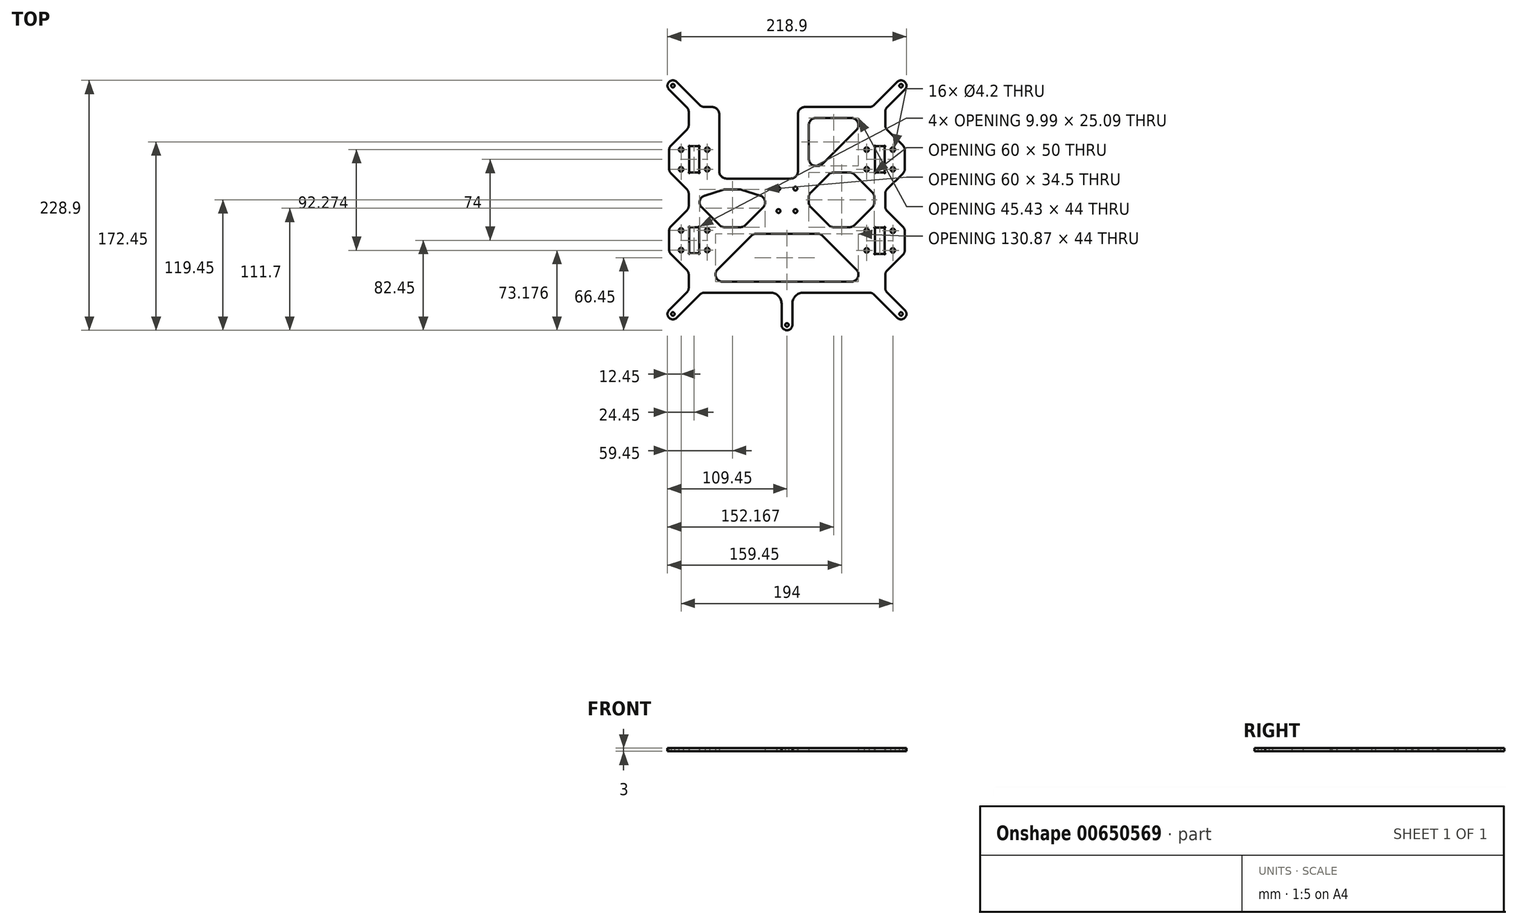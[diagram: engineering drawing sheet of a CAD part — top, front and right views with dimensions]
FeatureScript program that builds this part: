
annotation { "Feature Type Name" : "Feature", "Feature Type Description" : "" }
export const myFeature = defineFeature(function(context is Context, id is Id, definition is map)
    precondition{}
    {
        {
            var Q0;
            Q0=qCreatedBy(makeId("Top.planeOp"),FACE);
            var sketch = newSketch(context, id + "F0", { "sketchPlane" : qUnion([Q0])});
            skLineSegment(sketch, "E0", {"start": v(-106.24, 49.76) * mm, "end": v(-91.76, 64.24) * mm});
            skArc(sketch, "E1", {"start": v(-91.76, 64.24) * mm, "mid": v(-90.46, 66.19) * mm, "end": v(-90, 68.49) * mm});
            skLineSegment(sketch, "E2", {"start": v(-90, 68.49) * mm, "end": v(-90, 80.51) * mm});
            skArc(sketch, "E3", {"start": v(-90, 80.51) * mm, "mid": v(-90.46, 82.81) * mm, "end": v(-91.76, 84.76) * mm});
            skLineSegment(sketch, "E4", {"start": v(-91.76, 84.76) * mm, "end": v(-108, 101) * mm});
            skArc(sketch, "E5", {"start": v(-101, 108) * mm, "mid": v(-108, 108) * mm, "end": v(-108, 101) * mm});
            skLineSegment(sketch, "E6", {"start": v(-101, 108) * mm, "end": v(-79.76, 86.76) * mm});
            skArc(sketch, "E7", {"start": v(-79.76, 86.76) * mm, "mid": v(-77.81, 85.46) * mm, "end": v(-75.51, 85) * mm});
            skLineSegment(sketch, "E8", {"start": v(16.6, 85) * mm, "end": v(75.51, 85) * mm});
            skArc(sketch, "E9", {"start": v(75.51, 85) * mm, "mid": v(77.81, 85.46) * mm, "end": v(79.76, 86.76) * mm});
            skLineSegment(sketch, "E10", {"start": v(79.76, 86.76) * mm, "end": v(101, 108) * mm});
            skArc(sketch, "E11", {"start": v(108, 101) * mm, "mid": v(108, 108) * mm, "end": v(101, 108) * mm});
            skLineSegment(sketch, "E12", {"start": v(108, 101) * mm, "end": v(91.76, 84.76) * mm});
            skLineSegment(sketch, "E13", {"start": v(91.76, -84.76) * mm, "end": v(108, -101) * mm});
            skArc(sketch, "E14", {"start": v(101, -108) * mm, "mid": v(108, -108) * mm, "end": v(108, -101) * mm});
            skLineSegment(sketch, "E15", {"start": v(101, -108) * mm, "end": v(79.76, -86.76) * mm});
            skArc(sketch, "E16", {"start": v(79.76, -86.76) * mm, "mid": v(77.81, -85.46) * mm, "end": v(75.51, -85) * mm});
            skLineSegment(sketch, "E17", {"start": v(75.51, -85) * mm, "end": v(14.95, -85) * mm});
            skArc(sketch, "E18", {"start": v(-75.51, -85) * mm, "mid": v(-77.81, -85.46) * mm, "end": v(-79.76, -86.76) * mm});
            skLineSegment(sketch, "E19", {"start": v(-79.76, -86.76) * mm, "end": v(-101, -108) * mm});
            skArc(sketch, "E20", {"start": v(-108, -101) * mm, "mid": v(-108, -108) * mm, "end": v(-101, -108) * mm});
            skLineSegment(sketch, "E21", {"start": v(-108, -101) * mm, "end": v(-91.76, -84.76) * mm});
            skArc(sketch, "E22", {"start": v(-91.76, -84.76) * mm, "mid": v(-90.46, -82.81) * mm, "end": v(-90, -80.51) * mm});
            skLineSegment(sketch, "E23", {"start": v(-90, -80.51) * mm, "end": v(-90, -68.49) * mm});
            skArc(sketch, "E24", {"start": v(-90, -68.49) * mm, "mid": v(-90.46, -66.19) * mm, "end": v(-91.76, -64.24) * mm});
            skLineSegment(sketch, "E25", {"start": v(-91.76, -64.24) * mm, "end": v(-106.24, -49.76) * mm});
            skArc(sketch, "E26", {"start": v(-108, -45.51) * mm, "mid": v(-107.54, -47.81) * mm, "end": v(-106.24, -49.76) * mm});
            skLineSegment(sketch, "E27", {"start": v(-108, -45.51) * mm, "end": v(-108, -28.49) * mm});
            skArc(sketch, "E28", {"start": v(-106.24, -24.24) * mm, "mid": v(-107.54, -26.19) * mm, "end": v(-108, -28.49) * mm});
            skLineSegment(sketch, "E29", {"start": v(-106.24, -24.24) * mm, "end": v(-91.76, -9.76) * mm});
            skArc(sketch, "E30", {"start": v(-91.76, -9.76) * mm, "mid": v(-90.46, -7.81) * mm, "end": v(-90, -5.51) * mm});
            skLineSegment(sketch, "E31", {"start": v(-90, -5.51) * mm, "end": v(-90, 5.51) * mm});
            skArc(sketch, "E32", {"start": v(-90, 5.51) * mm, "mid": v(-90.46, 7.81) * mm, "end": v(-91.76, 9.76) * mm});
            skLineSegment(sketch, "E33", {"start": v(-91.76, 9.76) * mm, "end": v(-106.24, 24.24) * mm});
            skArc(sketch, "E34", {"start": v(-108, 28.49) * mm, "mid": v(-107.54, 26.19) * mm, "end": v(-106.24, 24.24) * mm});
            skLineSegment(sketch, "E35", {"start": v(-108, 28.49) * mm, "end": v(-108, 45.51) * mm});
            skArc(sketch, "E36", {"start": v(-106.24, 49.76) * mm, "mid": v(-107.54, 47.81) * mm, "end": v(-108, 45.51) * mm});
            skLineSegment(sketch, "E37", {"start": v(32.73, -32.93) * mm, "end": v(63.53, -63.73) * mm});
            skArc(sketch, "E38", {"start": v(58.87, -75) * mm, "mid": v(64.96, -70.93) * mm, "end": v(63.53, -63.73) * mm});
            skLineSegment(sketch, "E39", {"start": v(58.87, -75) * mm, "end": v(-58.87, -75) * mm});
            skArc(sketch, "E40", {"start": v(-63.53, -63.73) * mm, "mid": v(-64.96, -70.93) * mm, "end": v(-58.87, -75) * mm});
            skLineSegment(sketch, "E41", {"start": v(-63.53, -63.73) * mm, "end": v(-32.73, -32.93) * mm});
            skArc(sketch, "E42", {"start": v(-28.07, -31) * mm, "mid": v(-30.6, -31.5) * mm, "end": v(-32.73, -32.93) * mm});
            skLineSegment(sketch, "E43", {"start": v(-28.07, -31) * mm, "end": v(28.07, -31) * mm});
            skArc(sketch, "E44", {"start": v(32.73, -32.93) * mm, "mid": v(30.6, -31.5) * mm, "end": v(28.07, -31) * mm});
            skLineSegment(sketch, "E45", {"start": v(-55.4, 19.5) * mm, "end": v(3.4, 19.5) * mm});
            skLineSegment(sketch, "E46", {"start": v(-20, -2.35) * mm, "end": v(-20, -2.51) * mm});
            skArc(sketch, "E47", {"start": v(-21.76, -6.76) * mm, "mid": v(-20.46, -4.81) * mm, "end": v(-20, -2.51) * mm});
            skLineSegment(sketch, "E48", {"start": v(-21.76, -6.76) * mm, "end": v(-38.24, -23.24) * mm});
            skArc(sketch, "E49", {"start": v(-42.49, -25) * mm, "mid": v(-40.19, -24.54) * mm, "end": v(-38.24, -23.24) * mm});
            skLineSegment(sketch, "E50", {"start": v(-42.49, -25) * mm, "end": v(-57.51, -25) * mm});
            skArc(sketch, "E51", {"start": v(-61.76, -23.24) * mm, "mid": v(-59.81, -24.54) * mm, "end": v(-57.51, -25) * mm});
            skLineSegment(sketch, "E52", {"start": v(-61.76, -23.24) * mm, "end": v(-78.24, -6.76) * mm});
            skArc(sketch, "E53", {"start": v(-80, -2.51) * mm, "mid": v(-79.54, -4.81) * mm, "end": v(-78.24, -6.76) * mm});
            skLineSegment(sketch, "E54", {"start": v(-80, -2.51) * mm, "end": v(-80, -2.35) * mm});
            skLineSegment(sketch, "E55", {"start": v(38.24, -23.24) * mm, "end": v(21.76, -6.76) * mm});
            skArc(sketch, "E56", {"start": v(20, -2.51) * mm, "mid": v(20.46, -4.81) * mm, "end": v(21.76, -6.76) * mm});
            skLineSegment(sketch, "E57", {"start": v(20, -2.51) * mm, "end": v(20, 2.51) * mm});
            skArc(sketch, "E58", {"start": v(21.76, 6.76) * mm, "mid": v(20.46, 4.81) * mm, "end": v(20, 2.51) * mm});
            skLineSegment(sketch, "E59", {"start": v(21.76, 6.76) * mm, "end": v(38.24, 23.24) * mm});
            skArc(sketch, "E60", {"start": v(42.49, 25) * mm, "mid": v(40.19, 24.54) * mm, "end": v(38.24, 23.24) * mm});
            skArc(sketch, "E61", {"start": v(38.24, -23.24) * mm, "mid": v(40.19, -24.54) * mm, "end": v(42.49, -25) * mm});
            skLineSegment(sketch, "E62", {"start": v(-88.63, -49.05) * mm, "end": v(-81.37, -49.05) * mm});
            skLineSegment(sketch, "E63", {"start": v(-89.5, 48.18) * mm, "end": v(-89.5, 25.82) * mm});
            skArc(sketch, "E64", {"start": v(-89.75, 25.38) * mm, "mid": v(-89.57, 25.57) * mm, "end": v(-89.5, 25.82) * mm});
            skArc(sketch, "E65", {"start": v(-89.75, 25.38) * mm, "mid": v(-89.85, 24.6) * mm, "end": v(-89.07, 24.7) * mm});
            skArc(sketch, "E66", {"start": v(-88.63, 24.95) * mm, "mid": v(-88.88, 24.88) * mm, "end": v(-89.07, 24.7) * mm});
            skLineSegment(sketch, "E67", {"start": v(-88.63, 24.95) * mm, "end": v(-81.37, 24.95) * mm});
            skArc(sketch, "E68", {"start": v(-80.93, 24.7) * mm, "mid": v(-81.12, 24.88) * mm, "end": v(-81.37, 24.95) * mm});
            skArc(sketch, "E69", {"start": v(-80.93, 24.7) * mm, "mid": v(-80.15, 24.6) * mm, "end": v(-80.25, 25.38) * mm});
            skArc(sketch, "E70", {"start": v(-80.5, 25.82) * mm, "mid": v(-80.43, 25.57) * mm, "end": v(-80.25, 25.38) * mm});
            skLineSegment(sketch, "E71", {"start": v(-80.5, 25.82) * mm, "end": v(-80.5, 48.18) * mm});
            skArc(sketch, "E72", {"start": v(-80.25, 48.62) * mm, "mid": v(-80.43, 48.43) * mm, "end": v(-80.5, 48.18) * mm});
            skArc(sketch, "E73", {"start": v(-80.25, 48.62) * mm, "mid": v(-80.15, 49.4) * mm, "end": v(-80.93, 49.3) * mm});
            skArc(sketch, "E74", {"start": v(-81.37, 49.05) * mm, "mid": v(-81.12, 49.12) * mm, "end": v(-80.93, 49.3) * mm});
            skLineSegment(sketch, "E75", {"start": v(-81.37, 49.05) * mm, "end": v(-88.63, 49.05) * mm});
            skArc(sketch, "E76", {"start": v(-89.07, 49.3) * mm, "mid": v(-88.88, 49.12) * mm, "end": v(-88.63, 49.05) * mm});
            skArc(sketch, "E77", {"start": v(-89.07, 49.3) * mm, "mid": v(-89.85, 49.4) * mm, "end": v(-89.75, 48.62) * mm});
            skArc(sketch, "E78", {"start": v(-89.5, 48.18) * mm, "mid": v(-89.57, 48.43) * mm, "end": v(-89.75, 48.62) * mm});
            skCircle(sketch, "E79", {"center": v(-104.5, -104.5) * mm, "radius": 1.6 * mm});
            skCircle(sketch, "E80", {"center": v(-104.5, 104.5) * mm, "radius": 1.6 * mm});
            skCircle(sketch, "E81", {"center": v(-97, -28) * mm, "radius": 2.1 * mm});
            skCircle(sketch, "E82", {"center": v(-97, 28) * mm, "radius": 2.1 * mm});
            skCircle(sketch, "E83", {"center": v(-73, -28) * mm, "radius": 2.1 * mm});
            skCircle(sketch, "E84", {"center": v(-7.75, -10.25) * mm, "radius": 1.75 * mm});
            skCircle(sketch, "E85", {"center": v(7.75, -10.25) * mm, "radius": 1.75 * mm});
            skCircle(sketch, "E86", {"center": v(104.5, -104.5) * mm, "radius": 1.6 * mm});
            skCircle(sketch, "E87", {"center": v(104.5, 104.5) * mm, "radius": 1.6 * mm});
            skLineSegment(sketch, "E88", {"start": v(-89.5, -25.82) * mm, "end": v(-89.5, -48.18) * mm});
            skArc(sketch, "E89", {"start": v(-89.75, -48.62) * mm, "mid": v(-89.57, -48.43) * mm, "end": v(-89.5, -48.18) * mm});
            skArc(sketch, "E90", {"start": v(-89.75, -48.62) * mm, "mid": v(-89.85, -49.4) * mm, "end": v(-89.07, -49.3) * mm});
            skArc(sketch, "E91", {"start": v(-88.63, -49.05) * mm, "mid": v(-88.88, -49.12) * mm, "end": v(-89.07, -49.3) * mm});
            skArc(sketch, "E92", {"start": v(-80.93, -49.3) * mm, "mid": v(-81.12, -49.12) * mm, "end": v(-81.37, -49.05) * mm});
            skArc(sketch, "E93", {"start": v(-80.93, -49.3) * mm, "mid": v(-80.15, -49.4) * mm, "end": v(-80.25, -48.62) * mm});
            skArc(sketch, "E94", {"start": v(-80.5, -48.18) * mm, "mid": v(-80.43, -48.43) * mm, "end": v(-80.25, -48.62) * mm});
            skLineSegment(sketch, "E95", {"start": v(-80.5, -48.18) * mm, "end": v(-80.5, -25.82) * mm});
            skArc(sketch, "E96", {"start": v(-80.25, -25.38) * mm, "mid": v(-80.43, -25.57) * mm, "end": v(-80.5, -25.82) * mm});
            skArc(sketch, "E97", {"start": v(-80.25, -25.38) * mm, "mid": v(-80.15, -24.6) * mm, "end": v(-80.93, -24.7) * mm});
            skArc(sketch, "E98", {"start": v(-81.37, -24.95) * mm, "mid": v(-81.12, -24.88) * mm, "end": v(-80.93, -24.7) * mm});
            skLineSegment(sketch, "E99", {"start": v(-81.37, -24.95) * mm, "end": v(-88.63, -24.95) * mm});
            skArc(sketch, "E100", {"start": v(-89.07, -24.7) * mm, "mid": v(-88.88, -24.88) * mm, "end": v(-88.63, -24.95) * mm});
            skArc(sketch, "E101", {"start": v(-89.07, -24.7) * mm, "mid": v(-89.85, -24.6) * mm, "end": v(-89.75, -25.38) * mm});
            skArc(sketch, "E102", {"start": v(-89.5, -25.82) * mm, "mid": v(-89.57, -25.57) * mm, "end": v(-89.75, -25.38) * mm});
            skCircle(sketch, "E103", {"center": v(-7.75, 10.25) * mm, "radius": 1.6 * mm});
            skCircle(sketch, "E104", {"center": v(7.75, 10.25) * mm, "radius": 1.75 * mm});
            skArc(sketch, "E105", {"start": v(28.07, 31) * mm, "mid": v(30.6, 31.5) * mm, "end": v(32.73, 32.93) * mm});
            skLineSegment(sketch, "E106", {"start": v(28.07, 31) * mm, "end": v(26.6, 31) * mm});
            skArc(sketch, "E107", {"start": v(63.53, 63.73) * mm, "mid": v(64.96, 70.93) * mm, "end": v(58.87, 75) * mm});
            skLineSegment(sketch, "E108", {"start": v(63.53, 63.73) * mm, "end": v(32.73, 32.93) * mm});
            skLineSegment(sketch, "E109", {"start": v(26.6, 75) * mm, "end": v(58.87, 75) * mm});
            skLineSegment(sketch, "E110", {"start": v(106.24, 49.76) * mm, "end": v(91.76, 64.24) * mm});
            skArc(sketch, "E111", {"start": v(90, 68.49) * mm, "mid": v(90.46, 66.19) * mm, "end": v(91.76, 64.24) * mm});
            skArc(sketch, "E112", {"start": v(91.76, -64.7) * mm, "mid": v(90.46, -66.64) * mm, "end": v(90, -68.94) * mm});
            skLineSegment(sketch, "E113", {"start": v(91.76, -64.7) * mm, "end": v(106.24, -50.2) * mm});
            skArc(sketch, "E114", {"start": v(106.24, -50.2) * mm, "mid": v(107.54, -48.26) * mm, "end": v(108, -45.97) * mm});
            skLineSegment(sketch, "E115", {"start": v(108, -45.97) * mm, "end": v(108, -28.94) * mm});
            skArc(sketch, "E116", {"start": v(108, -28.94) * mm, "mid": v(107.54, -26.64) * mm, "end": v(106.24, -24.7) * mm});
            skLineSegment(sketch, "E117", {"start": v(106.24, -24.7) * mm, "end": v(91.76, -10.2) * mm});
            skArc(sketch, "E118", {"start": v(90, -5.97) * mm, "mid": v(90.46, -8.26) * mm, "end": v(91.76, -10.2) * mm});
            skLineSegment(sketch, "E119", {"start": v(90, -5.97) * mm, "end": v(90, 5.51) * mm});
            skArc(sketch, "E120", {"start": v(91.76, 9.76) * mm, "mid": v(90.46, 7.81) * mm, "end": v(90, 5.51) * mm});
            skLineSegment(sketch, "E121", {"start": v(91.76, 9.76) * mm, "end": v(106.24, 24.24) * mm});
            skArc(sketch, "E122", {"start": v(106.24, 24.24) * mm, "mid": v(107.54, 26.19) * mm, "end": v(108, 28.49) * mm});
            skLineSegment(sketch, "E123", {"start": v(108, 28.49) * mm, "end": v(108, 45.51) * mm});
            skArc(sketch, "E124", {"start": v(108, 45.51) * mm, "mid": v(107.54, 47.81) * mm, "end": v(106.24, 49.76) * mm});
            skArc(sketch, "E125", {"start": v(78.24, -6.76) * mm, "mid": v(79.54, -4.81) * mm, "end": v(80, -2.51) * mm});
            skLineSegment(sketch, "E126", {"start": v(80, -2.51) * mm, "end": v(80, 2.51) * mm});
            skArc(sketch, "E127", {"start": v(80, 2.51) * mm, "mid": v(79.54, 4.81) * mm, "end": v(78.24, 6.76) * mm});
            skLineSegment(sketch, "E128", {"start": v(88.63, -49.47) * mm, "end": v(81.37, -49.47) * mm});
            skLineSegment(sketch, "E129", {"start": v(89.5, 48.18) * mm, "end": v(89.5, 25.82) * mm});
            skArc(sketch, "E130", {"start": v(89.5, 25.82) * mm, "mid": v(89.57, 25.57) * mm, "end": v(89.75, 25.38) * mm});
            skArc(sketch, "E131", {"start": v(89.07, 24.7) * mm, "mid": v(89.85, 24.6) * mm, "end": v(89.75, 25.38) * mm});
            skArc(sketch, "E132", {"start": v(89.07, 24.7) * mm, "mid": v(88.88, 24.88) * mm, "end": v(88.63, 24.95) * mm});
            skLineSegment(sketch, "E133", {"start": v(88.63, 24.95) * mm, "end": v(81.37, 24.95) * mm});
            skArc(sketch, "E134", {"start": v(81.37, 24.95) * mm, "mid": v(81.12, 24.88) * mm, "end": v(80.93, 24.7) * mm});
            skArc(sketch, "E135", {"start": v(80.25, 25.38) * mm, "mid": v(80.15, 24.6) * mm, "end": v(80.93, 24.7) * mm});
            skArc(sketch, "E136", {"start": v(80.25, 25.38) * mm, "mid": v(80.43, 25.57) * mm, "end": v(80.5, 25.82) * mm});
            skLineSegment(sketch, "E137", {"start": v(80.5, 25.82) * mm, "end": v(80.5, 48.18) * mm});
            skArc(sketch, "E138", {"start": v(80.5, 48.18) * mm, "mid": v(80.43, 48.43) * mm, "end": v(80.25, 48.62) * mm});
            skArc(sketch, "E139", {"start": v(80.93, 49.3) * mm, "mid": v(80.15, 49.4) * mm, "end": v(80.25, 48.62) * mm});
            skArc(sketch, "E140", {"start": v(80.93, 49.3) * mm, "mid": v(81.12, 49.12) * mm, "end": v(81.37, 49.05) * mm});
            skLineSegment(sketch, "E141", {"start": v(81.37, 49.05) * mm, "end": v(88.63, 49.05) * mm});
            skArc(sketch, "E142", {"start": v(88.63, 49.05) * mm, "mid": v(88.88, 49.12) * mm, "end": v(89.07, 49.3) * mm});
            skArc(sketch, "E143", {"start": v(89.75, 48.62) * mm, "mid": v(89.85, 49.4) * mm, "end": v(89.07, 49.3) * mm});
            skArc(sketch, "E144", {"start": v(89.75, 48.62) * mm, "mid": v(89.57, 48.43) * mm, "end": v(89.5, 48.18) * mm});
            skCircle(sketch, "E145", {"center": v(97, -28.4) * mm, "radius": 2.1 * mm});
            skCircle(sketch, "E146", {"center": v(97, 46) * mm, "radius": 2.1 * mm});
            skLineSegment(sketch, "E147", {"start": v(89.5, -26.23) * mm, "end": v(89.5, -48.6) * mm});
            skArc(sketch, "E148", {"start": v(89.5, -48.6) * mm, "mid": v(89.57, -48.85) * mm, "end": v(89.75, -49.03) * mm});
            skArc(sketch, "E149", {"start": v(89.07, -49.72) * mm, "mid": v(89.85, -49.82) * mm, "end": v(89.75, -49.03) * mm});
            skArc(sketch, "E150", {"start": v(89.07, -49.72) * mm, "mid": v(88.88, -49.53) * mm, "end": v(88.63, -49.47) * mm});
            skArc(sketch, "E151", {"start": v(81.37, -49.47) * mm, "mid": v(81.12, -49.53) * mm, "end": v(80.93, -49.72) * mm});
            skArc(sketch, "E152", {"start": v(80.25, -49.03) * mm, "mid": v(80.15, -49.82) * mm, "end": v(80.93, -49.72) * mm});
            skArc(sketch, "E153", {"start": v(80.25, -49.03) * mm, "mid": v(80.43, -48.85) * mm, "end": v(80.5, -48.6) * mm});
            skLineSegment(sketch, "E154", {"start": v(80.5, -48.6) * mm, "end": v(80.5, -26.23) * mm});
            skArc(sketch, "E155", {"start": v(80.5, -26.23) * mm, "mid": v(80.43, -25.98) * mm, "end": v(80.25, -25.8) * mm});
            skArc(sketch, "E156", {"start": v(80.93, -25.12) * mm, "mid": v(80.15, -25.01) * mm, "end": v(80.25, -25.8) * mm});
            skArc(sketch, "E157", {"start": v(80.93, -25.12) * mm, "mid": v(81.12, -25.3) * mm, "end": v(81.37, -25.37) * mm});
            skLineSegment(sketch, "E158", {"start": v(81.37, -25.37) * mm, "end": v(88.63, -25.37) * mm});
            skArc(sketch, "E159", {"start": v(88.63, -25.37) * mm, "mid": v(88.88, -25.3) * mm, "end": v(89.07, -25.12) * mm});
            skArc(sketch, "E160", {"start": v(89.75, -25.8) * mm, "mid": v(89.85, -25.01) * mm, "end": v(89.07, -25.12) * mm});
            skArc(sketch, "E161", {"start": v(89.75, -25.8) * mm, "mid": v(89.57, -25.98) * mm, "end": v(89.5, -26.23) * mm});
            skLineSegment(sketch, "E162", {"start": v(78.24, 6.76) * mm, "end": v(61.76, 23.24) * mm});
            skArc(sketch, "E163", {"start": v(61.76, 23.24) * mm, "mid": v(59.81, 24.54) * mm, "end": v(57.51, 25) * mm});
            skArc(sketch, "E164", {"start": v(57.51, -25) * mm, "mid": v(59.81, -24.54) * mm, "end": v(61.76, -23.24) * mm});
            skLineSegment(sketch, "E165", {"start": v(61.76, -23.24) * mm, "end": v(78.24, -6.76) * mm});
            skCircle(sketch, "E166", {"center": v(73, -28.4) * mm, "radius": 2.1 * mm});
            skCircle(sketch, "E167", {"center": v(73, 46) * mm, "radius": 2.1 * mm});
            skLineSegment(sketch, "E168", {"start": v(57.51, 25) * mm, "end": v(42.49, 25) * mm});
            skLineSegment(sketch, "E169", {"start": v(42.49, -25) * mm, "end": v(57.51, -25) * mm});
            skLineSegment(sketch, "E170", {"start": v(90, 68.49) * mm, "end": v(90, 80.51) * mm});
            skLineSegment(sketch, "E171", {"start": v(90, -80.51) * mm, "end": v(90, -68.94) * mm});
            skArc(sketch, "E172", {"start": v(90, -80.51) * mm, "mid": v(90.46, -82.81) * mm, "end": v(91.76, -84.76) * mm});
            skArc(sketch, "E173", {"start": v(91.76, 84.76) * mm, "mid": v(90.46, 82.81) * mm, "end": v(90, 80.51) * mm});
            skArc(sketch, "E174", {"start": v(-4.95, -114.5) * mm, "mid": v(0, -119.45) * mm, "end": v(4.95, -114.5) * mm});
            skCircle(sketch, "E175", {"center": v(0, -114.5) * mm, "radius": 1.6 * mm});
            skLineSegment(sketch, "E176", {"start": v(4.95, -95) * mm, "end": v(4.95, -114.5) * mm});
            skLineSegment(sketch, "E177", {"start": v(-4.95, -114.5) * mm, "end": v(-4.95, -95) * mm});
            skArc(sketch, "E178", {"start": v(14.95, -85) * mm, "mid": v(7.88, -87.93) * mm, "end": v(4.95, -95) * mm});
            skLineSegment(sketch, "E179", {"start": v(-75.51, -85) * mm, "end": v(-14.95, -85) * mm});
            skArc(sketch, "E180", {"start": v(-4.95, -95) * mm, "mid": v(-7.88, -87.93) * mm, "end": v(-14.95, -85) * mm});
            skPoint(sketch, "E181", {"position": v(0, 0) * mm});
            skLineSegment(sketch, "E182", {"start": v(10, 78.4) * mm, "end": v(10, 26.1) * mm});
            skLineSegment(sketch, "E183.0", {"start": v(20, 68.4) * mm, "end": v(20, 37.6) * mm});
            skLineSegment(sketch, "E184.0", {"start": v(-62, 78.4) * mm, "end": v(-62, 26.1) * mm});
            skArc(sketch, "E185.filletArc", {"start": v(26.6, 75) * mm, "mid": v(21.93, 73.07) * mm, "end": v(20, 68.4) * mm});
            skArc(sketch, "E186.filletArc", {"start": v(3.4, 19.5) * mm, "mid": v(8.07, 21.43) * mm, "end": v(10, 26.1) * mm});
            skArc(sketch, "E187.filletArc", {"start": v(16.6, 85) * mm, "mid": v(11.93, 83.07) * mm, "end": v(10, 78.4) * mm});
            skLineSegment(sketch, "E188", {"start": v(-75.51, 85) * mm, "end": v(-68.6, 85) * mm});
            skPoint(sketch, "E189.visualSharp", {"position": v(-62, 85) * mm});
            skArc(sketch, "E189.filletArc", {"start": v(-62, 78.4) * mm, "mid": v(-63.93, 83.07) * mm, "end": v(-68.6, 85) * mm});
            skArc(sketch, "E190.filletArc", {"start": v(-62, 26.1) * mm, "mid": v(-60.07, 21.43) * mm, "end": v(-55.4, 19.5) * mm});
            skArc(sketch, "E191.filletArc", {"start": v(20, 37.6) * mm, "mid": v(21.93, 32.93) * mm, "end": v(26.6, 31) * mm});
            skLineSegment(sketch, "E192", {"start": v(-127.88, 46) * mm, "end": v(127.39, 46) * mm, "construction": true});
            skLineSegment(sketch, "E193.0", {"start": v(-127.88, 105) * mm, "end": v(127.39, 105) * mm, "construction": true});
            skLineSegment(sketch, "E194.0", {"start": v(-127.88, 28) * mm, "end": v(127.39, 28) * mm, "construction": true});
            skCircle(sketch, "E195", {"center": v(-97, 46) * mm, "radius": 2.1 * mm});
            skCircle(sketch, "E196", {"center": v(-73, 46) * mm, "radius": 2.1 * mm});
            skCircle(sketch, "E197", {"center": v(-73, 28) * mm, "radius": 2.1 * mm});
            skLineSegment(sketch, "E198", {"start": v(-43.49, 9.5) * mm, "end": v(-56.51, 9.5) * mm});
            skLineSegment(sketch, "E199", {"start": v(-75.36, 3.96) * mm, "end": v(-58.47, 9.2) * mm});
            skLineSegment(sketch, "E200", {"start": v(-41.53, 9.2) * mm, "end": v(-24.64, 3.96) * mm});
            skPoint(sketch, "E201.visualSharp", {"position": v(-80, 2.51) * mm});
            skArc(sketch, "E201.filletArc", {"start": v(-75.36, 3.96) * mm, "mid": v(-78.71, 1.57) * mm, "end": v(-80, -2.35) * mm});
            skPoint(sketch, "E202.visualSharp", {"position": v(-20, 2.51) * mm});
            skArc(sketch, "E202.filletArc", {"start": v(-20, -2.35) * mm, "mid": v(-21.29, 1.57) * mm, "end": v(-24.64, 3.96) * mm});
            skPoint(sketch, "E203.visualSharp", {"position": v(-57.51, 9.5) * mm});
            skArc(sketch, "E203.filletArc", {"start": v(-56.51, 9.5) * mm, "mid": v(-57.5, 9.43) * mm, "end": v(-58.47, 9.2) * mm});
            skPoint(sketch, "E204.visualSharp", {"position": v(-42.49, 9.5) * mm});
            skArc(sketch, "E204.filletArc", {"start": v(-41.53, 9.2) * mm, "mid": v(-42.5, 9.43) * mm, "end": v(-43.49, 9.5) * mm});
            skLineSegment(sketch, "E205", {"start": v(-85, 112.48) * mm, "end": v(-85, -138.02) * mm, "construction": true});
            skLineSegment(sketch, "E206", {"start": v(-97, 46) * mm, "end": v(-97, 28) * mm, "construction": true});
            skPoint(sketch, "E207", {"position": v(-108, 37) * mm});
            skPoint(sketch, "E208", {"position": v(-97, 37) * mm});
            skPoint(sketch, "E209", {"position": v(-89.5, 37) * mm});
            skPoint(sketch, "E210", {"position": v(-85, 49.05) * mm});
            skPoint(sketch, "E211", {"position": v(108, 37) * mm});
            skPoint(sketch, "E212", {"position": v(80.5, 37) * mm});
            skLineSegment(sketch, "E213", {"start": v(85, 124) * mm, "end": v(85, -126.5) * mm, "construction": true});
            skPoint(sketch, "E214", {"position": v(85, 49.05) * mm});
            skCircle(sketch, "E215", {"center": v(97, 28) * mm, "radius": 2.1 * mm});
            skCircle(sketch, "E216", {"center": v(73, 28) * mm, "radius": 2.1 * mm});
            skCircle(sketch, "E217", {"center": v(-97, -46) * mm, "radius": 2.1 * mm});
            skCircle(sketch, "E218", {"center": v(-73, -46) * mm, "radius": 2.1 * mm});
            skLineSegment(sketch, "E219", {"start": v(-97, -28) * mm, "end": v(-97, -46) * mm, "construction": true});
            skPoint(sketch, "E220", {"position": v(-97, -37) * mm});
            skPoint(sketch, "E221", {"position": v(-89.5, -37) * mm});
            skPoint(sketch, "E222", {"position": v(89.5, -37.42) * mm});
            skPoint(sketch, "E223", {"position": v(108, -37.45) * mm});
            skLineSegment(sketch, "E224", {"start": v(-126.11, -28) * mm, "end": v(126.33, -28.49) * mm, "construction": true});
            skLineSegment(sketch, "E225", {"start": v(-125.88, -45.9) * mm, "end": v(127.8, -46.38) * mm, "construction": true});
            skCircle(sketch, "E226", {"center": v(97, -46.27) * mm, "radius": 2.1 * mm});
            skCircle(sketch, "E227", {"center": v(73, -46.27) * mm, "radius": 2.1 * mm});
            skPoint(sketch, "E228", {"position": v(-108, -37) * mm});
            skLineSegment(sketch, "E229", {"start": v(-127.46, -37) * mm, "end": v(147.05, -37.53) * mm, "construction": true});
            skSolve(sketch);
        }
        {
            var Q0;
            Q0=makeQuery(id+"F0.imprint","IMPRINT",FACE,{"disambiguationData":[TD([[makeQuery(id+"F0.imprint","IMPRINT",EDGE,{"derivedFrom":sQuery(id+"F0.wireOp",EDGE,"E0")}),-1.0]])]});
            extrude(context, id + "F1", {"entities" : qUnion([Q0]), "depth" : 3 * mm, "offsetDistance" : 25 * mm});
        }
    });
